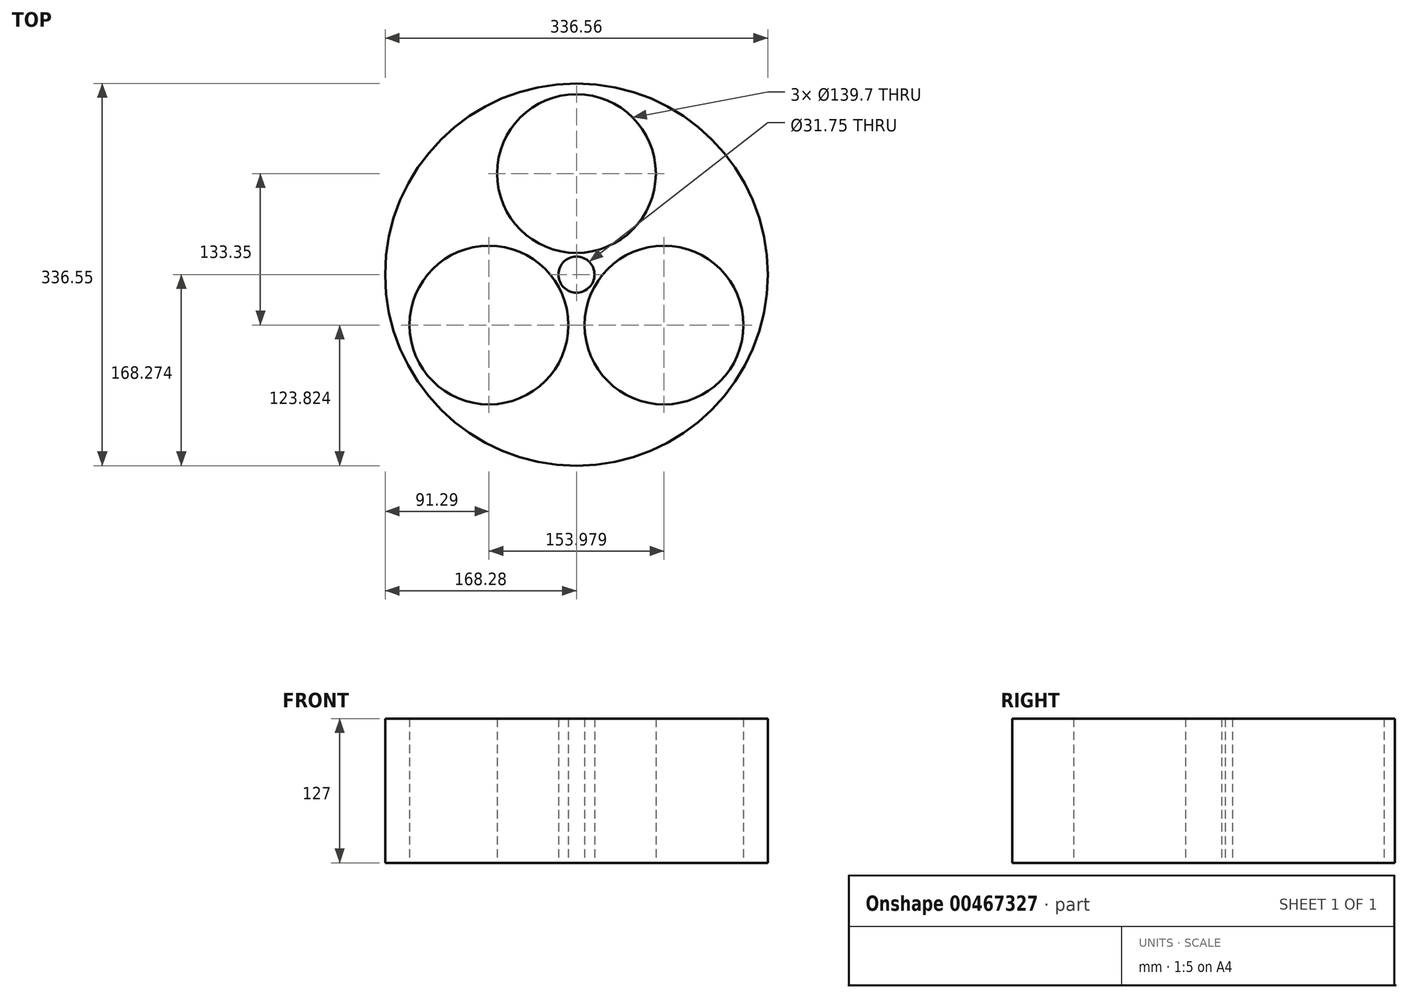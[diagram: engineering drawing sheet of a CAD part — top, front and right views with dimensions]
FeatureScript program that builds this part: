
annotation { "Feature Type Name" : "Feature", "Feature Type Description" : "" }
export const myFeature = defineFeature(function(context is Context, id is Id, definition is map)
    precondition{}
    {
        {
            var Q0;
            Q0=qCreatedBy(makeId("Top.planeOp"),FACE);
            var sketch = newSketch(context, id + "F0", { "sketchPlane" : qUnion([Q0])});
            skCircle(sketch, "E0", {"center": v(0, 84.64) * mm, "radius": 69.85 * mm});
            skCircle(sketch, "E1.1.0", {"center": v(-76.99, -48.7) * mm, "radius": 69.85 * mm});
            skCircle(sketch, "E1.2.0", {"center": v(76.99, -48.7) * mm, "radius": 69.85 * mm});
            skPoint(sketch, "E1.center", {"position": v(0, -4.26) * mm});
            skCircle(sketch, "E2", {"center": v(0, -4.26) * mm, "radius": 168.28 * mm});
            skCircle(sketch, "E3", {"center": v(0, -4.26) * mm, "radius": 88.9 * mm, "construction": true});
            skCircle(sketch, "E4", {"center": v(0, -4.26) * mm, "radius": 15.88 * mm});
            skSolve(sketch);
        }
        {
            var Q0;
            Q0=makeQuery(id+"F0.imprint","IMPRINT",FACE,{"disambiguationData":[TD([[makeQuery(id+"F0.imprint","IMPRINT",EDGE,{"derivedFrom":sQuery(id+"F0.wireOp",EDGE,"E0")}),-1.0]])]});
            extrude(context, id + "F1", {"entities" : qUnion([Q0]), "depth" : 127 * mm});
        }
    });
